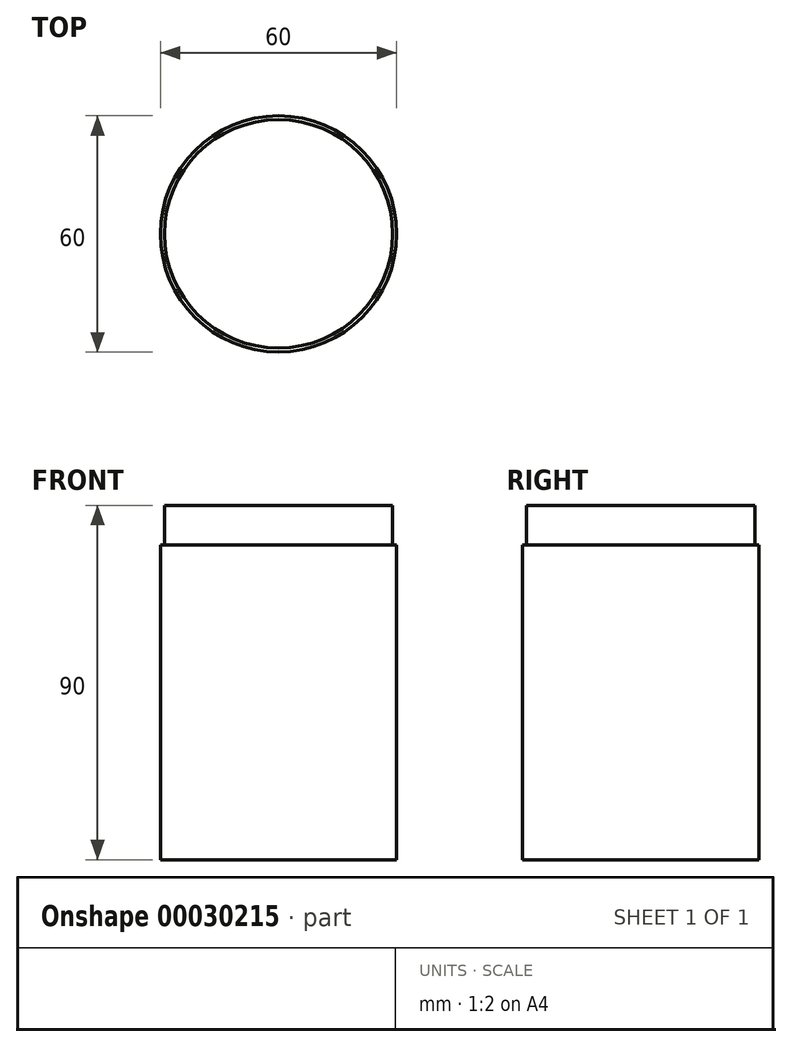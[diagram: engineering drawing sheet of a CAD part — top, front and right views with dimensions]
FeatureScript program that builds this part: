
annotation { "Feature Type Name" : "Feature", "Feature Type Description" : "" }
export const myFeature = defineFeature(function(context is Context, id is Id, definition is map)
    precondition{}
    {
        {
            var Q0;
            Q0=qCreatedBy(makeId("Top.planeOp"),FACE);
            var sketch = newSketch(context, id + "F0", { "sketchPlane" : qUnion([Q0])});
            skCircle(sketch, "E0", {"center": v(0, 0) * mm, "radius": 30 * mm});
            skSolve(sketch);
        }
        {
            var Q0;
            Q0=qCreatedBy(makeId("Top.planeOp"),FACE);
            var sketch = newSketch(context, id + "F1", { "sketchPlane" : qUnion([Q0])});
            skCircle(sketch, "E1", {"center": v(0, 0) * mm, "radius": 29 * mm});
            skSolve(sketch);
        }
        {
            var Q0;
            Q0 = qSketchRegion(id + "F0", true);
            extrude(context, id + "F2", {"entities" : qUnion([Q0]), "depth" : 80 * mm});
        }
        {
            var Q0;
            Q0 = qSketchRegion(id + "F1", true);
            extrude(context, id + "F3", {"entities" : qUnion([Q0]), "operationType" : NewBodyOperationType.ADD, "depth" : 90 * mm});
        }
    });
